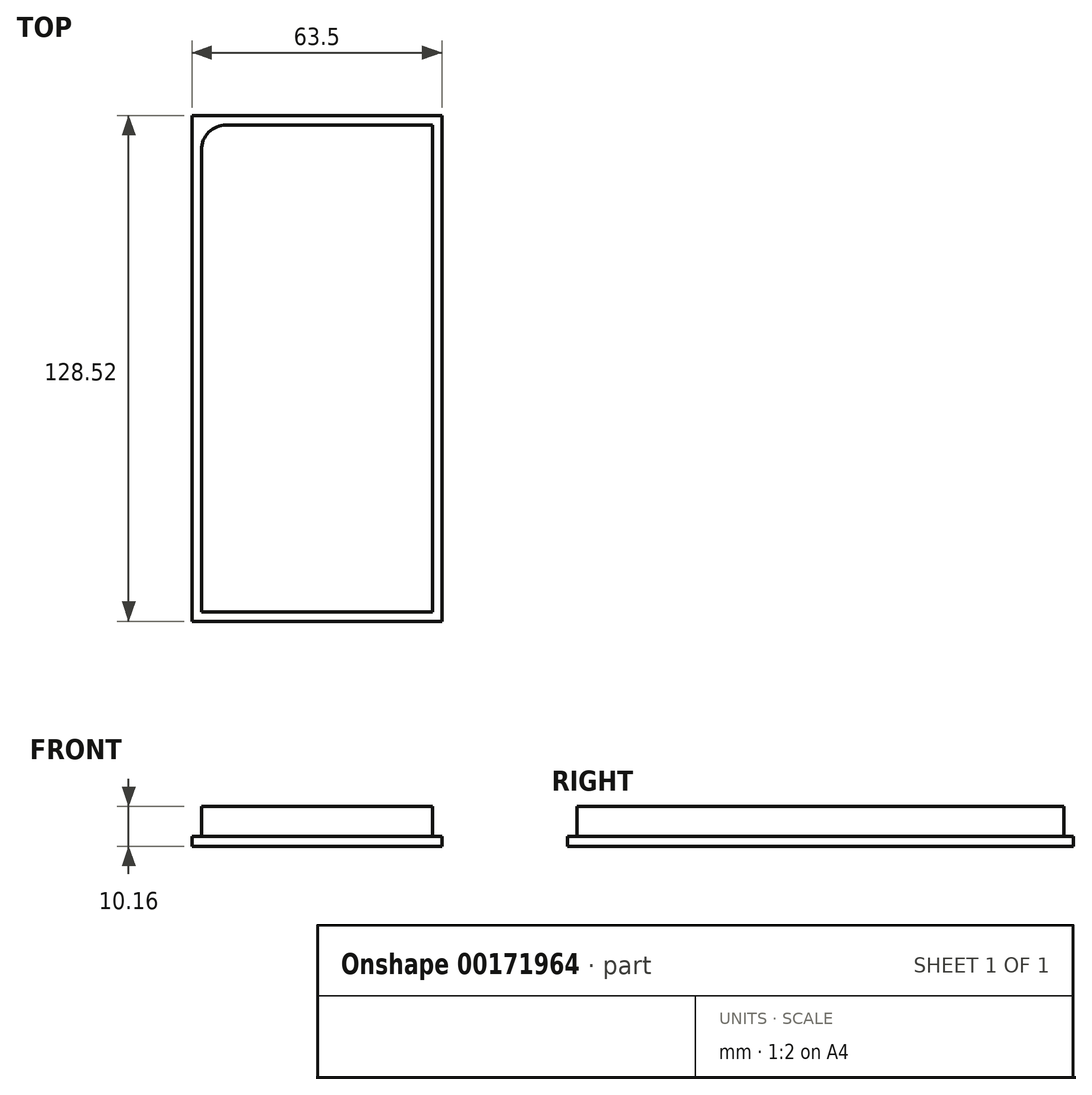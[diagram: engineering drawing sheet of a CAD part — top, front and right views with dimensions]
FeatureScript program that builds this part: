
annotation { "Feature Type Name" : "Feature", "Feature Type Description" : "" }
export const myFeature = defineFeature(function(context is Context, id is Id, definition is map)
    precondition{}
    {
        {
            var Q0;
            Q0=qCreatedBy(makeId("Top.planeOp"),FACE);
            var sketch = newSketch(context, id + "F0", { "sketchPlane" : qUnion([Q0])});
            skLineSegment(sketch, "E0.bottom", {"start": v(29.34, -61.85) * mm, "end": v(-29.34, -61.85) * mm});
            skLineSegment(sketch, "E0.top", {"start": v(29.34, 61.85) * mm, "end": v(-29.34, 61.85) * mm});
            skLineSegment(sketch, "E0.left", {"start": v(29.34, -61.85) * mm, "end": v(29.34, 61.85) * mm});
            skLineSegment(sketch, "E0.right", {"start": v(-29.34, -61.85) * mm, "end": v(-29.34, 61.85) * mm});
            skPoint(sketch, "E0.middle", {"position": v(0, 0) * mm});
            skLineSegment(sketch, "E1.bottom", {"start": v(31.75, -64.26) * mm, "end": v(-31.75, -64.26) * mm});
            skLineSegment(sketch, "E1.top", {"start": v(31.75, 64.26) * mm, "end": v(-31.75, 64.26) * mm});
            skLineSegment(sketch, "E1.left", {"start": v(31.75, -64.26) * mm, "end": v(31.75, 64.26) * mm});
            skLineSegment(sketch, "E1.right", {"start": v(-31.75, -64.26) * mm, "end": v(-31.75, 64.26) * mm});
            skSolve(sketch);
        }
        {
            var Q0;
            Q0 = qSketchRegion(id + "F0", true);
            var Q1;
            Q1=makeQuery(id+"F0.imprint","IMPRINT",FACE,{"disambiguationData":[TD([[makeQuery(id+"F0.imprint","IMPRINT",EDGE,{"derivedFrom":sQuery(id+"F0.wireOp",EDGE,"E0.bottom")}),-1.0]])]});
            extrude(context, id + "F1", {"entities" : qUnion([Q0, Q1]), "depth" : 2.54 * mm});
        }
        {
            var Q0;
            Q0=makeQuery(id+"F1.opExtrude","CAP_FACE",FACE,{"disambiguationData":[OSD([sQuery(id+"F0.wireOp",EDGE,"E1.bottom"),sQuery(id+"F0.wireOp",EDGE,"E1.top"),sQuery(id+"F0.wireOp",EDGE,"E1.left"),sQuery(id+"F0.wireOp",EDGE,"E1.right")])],"isStart":false});
            var sketch = newSketch(context, id + "F2", { "sketchPlane" : qUnion([Q0])});
            skLineSegment(sketch, "E2.bottom", {"start": v(29.34, -61.85) * mm, "end": v(-29.34, -61.85) * mm});
            skLineSegment(sketch, "E2.top", {"start": v(29.34, 61.85) * mm, "end": v(-22.99, 61.85) * mm});
            skLineSegment(sketch, "E2.left", {"start": v(29.34, -61.85) * mm, "end": v(29.34, 61.85) * mm});
            skLineSegment(sketch, "E2.right", {"start": v(-29.34, -61.85) * mm, "end": v(-29.34, 55.5) * mm});
            skPoint(sketch, "E2.middle", {"position": v(0, 0) * mm});
            skPoint(sketch, "E3.visualSharp", {"position": v(-29.34, 61.85) * mm});
            skArc(sketch, "E3.filletArc", {"start": v(-22.99, 61.85) * mm, "mid": v(-27.48, 59.99) * mm, "end": v(-29.34, 55.5) * mm});
            skSolve(sketch);
        }
        {
            var Q0;
            Q0 = qSketchRegion(id + "F2", true);
            extrude(context, id + "F3", {"entities" : qUnion([Q0]), "operationType" : NewBodyOperationType.ADD, "depth" : 7.62 * mm});
        }
    });
